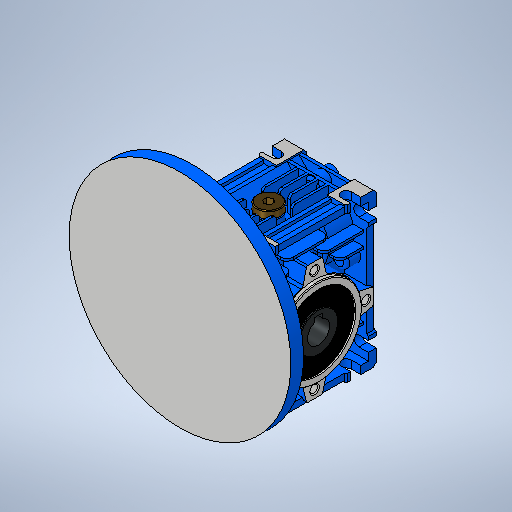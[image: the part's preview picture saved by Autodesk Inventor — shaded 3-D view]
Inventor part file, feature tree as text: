
AUTODESK INVENTOR PART (.ipt)
format: ipt  version: 2025.1 (Build 291241020, 241B)  size: 3,167,232 bytes
history: native  units: mm
features: extrude x72, sketch x64, projected_geometry x30, chamfer x22, fillet x17, mirror x13, other x8, hole x3, pattern_linear x1, revolve x1, sheet_metal_op x1
ambient origin geometry x8: Origin, YZ Plane, XZ Plane, XY Plane, X Axis, Y Axis, Z Axis, Center Point
bodies: Body1 (feature_tree), Body2 (feature_tree), Body3 (feature_tree)
feature tree (232):
  other  "Твердое тело1"
  extrude  "Выдавливание1"  Depth=63.0mm
  extrude  "Выдавливание2"  Depth=55.0mm
  extrude  "Выдавливание3"  Depth=15.0mm
  mirror  "Зеркальное отражение2"
  mirror  "Зеркальное отражение3"
  mirror  "Зеркальное отражение4"
  hole  "Отверстие1"  [1 undecoded]
  mirror  "Зеркальное отражение5"
  extrude  "Выдавливание4"  Depth=15.0mm
  extrude  "Выдавливание5"  Depth=15.0mm
  mirror  "Зеркальное отражение6"
  extrude  "Выдавливание6"  Depth=15.0mm
  mirror  "Зеркальное отражение7"
  chamfer  "Фаска1"  Distance=32.5mm
  extrude  "Выдавливание8"  Depth=10.0mm
  extrude  "Выдавливание9"  Depth=15.0mm
  fillet  "Сопряжение1"  Radius=1.0mm
  mirror  "Зеркальное отражение8"
  extrude  "Выдавливание10"  Depth=15.0mm
  extrude  "Выдавливание11"  Depth=15.0mm TaperAngle=360.0deg
  extrude  "Выдавливание12"  Depth=15.0mm TaperAngle=0.0deg
  chamfer  "Фаска2"  Distance=32.5mm
  chamfer  "Фаска3"  Distance=32.5mm
  extrude  "Выдавливание13"  Depth=15.0mm
  extrude  "Выдавливание14"  Depth=15.0mm
  chamfer  "Фаска4"  Distance=14.0mm
  extrude  "Выдавливание15"  Depth=5.0mm
  mirror  "Зеркальное отражение9"
  other  "РабПлоскость1"
  extrude  "Выдавливание16"  Depth=15.0mm
  extrude  "Выдавливание17"  Depth=15.0mm TaperAngle=0.0deg
  pattern_linear  "Прямоуг.массив1"  Spacing1=25.0mm  [1 undecoded]
  chamfer  "Фаска6"  Distance=47.0mm
  extrude  "Выдавливание18"  Depth=15.0mm TaperAngle=0.0deg
  chamfer  "Фаска7"  Distance=42.0mm
  fillet  "Сопряжение2"  Radius=42.0mm
  fillet  "Сопряжение3"  Radius=58.0mm
  fillet  "Сопряжение4"  Radius=1.0mm
  extrude  "Выдавливание19"  Depth=5.0mm
  chamfer  "Фаска8"  Distance=5.0mm
  chamfer  "Фаска9"  Distance=58.0mm
  chamfer  "Фаска10"  Distance=2.0mm Angle=45.0deg
  other  "РабОсь1"
  extrude  "Выдавливание20"  Depth=15.0mm TaperAngle=0.0deg
  extrude  "Выдавливание21"  Depth=15.0mm
  chamfer  "Фаска13"  Distance=1.5mm
  fillet  "Сопряжение7"  Radius=8.0mm
  extrude  "Выдавливание22"  Depth=15.0mm
  chamfer  "Фаска14"  Distance=4.0mm
  extrude  "Выдавливание23"  Depth=15.0mm TaperAngle=0.0deg
  extrude  "Выдавливание26"  Depth=15.0mm
  extrude  "Выдавливание27"  Depth=15.0mm TaperAngle=0.0deg
  chamfer  "Фаска15"  Distance=1.0mm
  extrude  "Выдавливание28"  Depth=15.0mm
  chamfer  "Фаска16"  Distance=1.0mm
  extrude  "Выдавливание29"  Depth=15.0mm TaperAngle=45.0deg
  chamfer  "Фаска17"  Distance=0.4mm Angle=45.0deg
  chamfer  "Фаска18"  Distance=20.0mm
  extrude  "Выдавливание30"  Depth=15.0mm TaperAngle=0.0deg
  mirror  "Зеркальное отражение10"
  extrude  "Выдавливание32"  Depth=15.0mm TaperAngle=0.0deg
  mirror  "Зеркальное отражение11"
  extrude  "Выдавливание33"  Depth=15.0mm TaperAngle=45.0deg
  extrude  "Выдавливание34"  Depth=15.0mm
  fillet  "Сопряжение8"  Radius=2.5mm
  extrude  "Выдавливание35"  Depth=15.0mm TaperAngle=0.0deg
  fillet  "Сопряжение10"  [1 undecoded]
  extrude  "Выдавливание36"  Depth=15.0mm
  fillet  "Сопряжение12"  Radius=1.5mm
  extrude  "Выдавливание37"  Depth=15.0mm TaperAngle=0.0deg
  extrude  "Выдавливание38"  Depth=15.0mm TaperAngle=0.0deg
  extrude  "Выдавливание39"  Depth=15.0mm
  chamfer  "Фаска19"  Distance=4.0mm Angle=45.0deg
  extrude  "Выдавливание40"  Depth=15.0mm TaperAngle=0.0deg
  sketch  "Эскиз45"
  extrude  "Выдавливание41"  Depth=15.0mm TaperAngle=45.0deg
  extrude  "Выдавливание42"  Depth=15.0mm
  extrude  "Выдавливание43"  Depth=15.0mm
  extrude  "Выдавливание44"  Depth=15.0mm
  extrude  "Выдавливание45"  Depth=15.0mm
  fillet  "Сопряжение13"  Radius=6.5mm
  other  "РабПлоскость2"
  extrude  "Выдавливание46"  Depth=15.0mm
  other  "РабПлоскость3"
  other  "РабПлоскость4"
  sketch  "Эскиз49"
  extrude  "Выдавливание47"  Depth=15.0mm
  extrude  "Выдавливание48"  Depth=15.0mm
  fillet  "Сопряжение14"  Radius=44.0mm
  extrude  "Выдавливание49"  Depth=15.0mm TaperAngle=0.0deg
  fillet  "Сопряжение15"  Radius=1.0mm
  extrude  "Выдавливание50"  Depth=15.0mm TaperAngle=45.0deg
  extrude  "Выдавливание51"  Depth=15.0mm TaperAngle=45.0deg
  extrude  "Выдавливание52"  Depth=15.0mm
  extrude  "Выдавливание53"  Depth=15.0mm
  extrude  "Выдавливание54"  Depth=4.0mm
  fillet  "Сопряжение16"  Radius=4.0mm
  extrude  "Выдавливание55"  Depth=4.0mm
  extrude  "Выдавливание56"  TaperAngle=120.0deg  [1 undecoded]
  chamfer  "Фаска20"  Angle=120.0deg  [1 undecoded]
  hole  "Отверстие2"  [1 undecoded]
  extrude  "Выдавливание57"  Depth=15.0mm
  chamfer  "Фаска21"  Distance=3.0mm
  extrude  "Выдавливание58"  Depth=15.0mm
  extrude  "Выдавливание59"  Depth=15.0mm
  extrude  "Выдавливание60"  Depth=15.0mm
  extrude  "Выдавливание61"  Depth=15.0mm
  extrude  "Выдавливание62"  Depth=15.0mm
  extrude  "Выдавливание63"  Depth=15.0mm TaperAngle=0.0deg
  extrude  "Выдавливание64"  Depth=15.0mm
  chamfer  "Фаска22"  Distance=1.0mm
  fillet  "Сопряжение17"  Radius=0.0001mm
  extrude  "Выдавливание65"  Depth=15.0mm TaperAngle=45.0deg
  mirror  "Зеркальное отражение13"
  extrude  "Выдавливание66"  Depth=15.0mm
  chamfer  "Фаска24"  Distance=17.75mm
  extrude  "Выдавливание67"  Depth=15.0mm TaperAngle=45.0deg
  chamfer  "Фаска25"  Distance=28.5mm
  extrude  "Выдавливание68"  Depth=15.0mm
  mirror  "Зеркальное отражение14"
  extrude  "Выдавливание69"  Depth=5.5mm
  chamfer  "Фаска26"  Distance=3.0mm
  extrude  "Выдавливание70"  Depth=15.0mm
  extrude  "Выдавливание72"  Depth=15.0mm TaperAngle=0.0deg
  fillet  "Сопряжение18"  Radius=2.0mm
  extrude  "Выдавливание73"  Depth=15.0mm TaperAngle=45.0deg
  fillet  "Сопряжение19"  Radius=32.0mm
  extrude  "Выдавливание74"  Depth=15.0mm TaperAngle=0.0deg
  fillet  "Сопряжение20"  Radius=0.5mm
  hole  "Отверстие4"  [1 undecoded]
  other  "РабПлоскость6"
  extrude  "Выдавливание76"  Depth=4.0mm
  mirror  "Зеркальное отражение15"
  fillet  "Сопряжение21"  Radius=4.0mm
  extrude  "Выдавливание77"  Depth=15.0mm TaperAngle=0.0deg
  extrude  "Выдавливание78"  Depth=15.0mm TaperAngle=45.0deg
  revolve  "Revolution1"  Angle=45.0deg
  sketch  "Эскиз1"
  sketch  "Sketch Circular Pattern1"  dims[d0=80.0mm d1=63.0mm]
  sketch  "Эскиз4"
  projected_geometry  "Спроецированная петля3"
  sketch  "Эскиз10"
  projected_geometry  "Спроецированная петля5"
  sketch  "Эскиз11"
  sketch  "Эскиз12"
  sketch  "Эскиз13"
  sketch  "Эскиз18"
  sketch  "Эскиз19"
  projected_geometry  "Спроецированная петля6"
  sketch  "Эскиз20"
  projected_geometry  "Спроецированная петля7"
  sketch  "Эскиз22"
  sketch  "Эскиз26"
  sketch  "Эскиз27"
  sketch  "Эскиз28"
  sketch  "Эскиз29"
  projected_geometry  "Спроецированная петля9"
  projected_geometry  "Спроецированная петля10"
  sketch  "Эскиз30"
  projected_geometry  "Спроецированная петля11"
  sketch  "Эскиз31"
  projected_geometry  "Спроецированная петля12"
  sketch  "Эскиз32"
  projected_geometry  "Спроецированная петля13"
  sketch  "Эскиз34"
  projected_geometry  "Спроецированная петля14"
  sketch  "Эскиз35"
  sketch  "Эскиз36"
  sketch  "Эскиз37"
  sketch  "Эскиз38"
  sketch  "Эскиз39"
  sketch  "Эскиз40"
  sketch  "Эскиз42"
  sketch  "Эскиз43"
  sketch  "Эскиз46"
  projected_geometry  "Спроецированная петля15"
  sketch  "Эскиз47"
  sketch  "Эскиз48"
  projected_geometry  "Спроецированная петля16"
  sketch  "Эскиз50"
  sketch  "Эскиз51"
  sketch  "Эскиз53"
  sketch  "Эскиз54"
  projected_geometry  "Спроецированная петля23"
  projected_geometry  "Спроецированная петля24"
  sketch  "Эскиз55"
  sketch  "Эскиз56"
  projected_geometry  "Спроецированная петля25"
  projected_geometry  "Спроецированная петля26"
  sketch  "Эскиз57"
  sketch  "Эскиз58"
  projected_geometry  "Спроецированная петля27"
  sketch  "Эскиз59"
  sketch  "Эскиз60"
  other  "Твердое тело4"
  sketch  "Эскиз61"
  sketch  "Эскиз62"
  projected_geometry  "Спроецированная петля28"
  projected_geometry  "Спроецированная петля29"
  sketch  "Эскиз63"
  sketch  "Эскиз64"
  sketch  "Sketch Circular Pattern2"  dims[d2=97.0mm d3=0.0mm d4=55.0mm]
  sketch  "Эскиз65"
  projected_geometry  "Спроецированная петля30"
  sketch  "Эскиз66"
  sketch  "Эскиз67"
  projected_geometry  "Спроецированная петля31"
  sketch  "Эскиз69"
  sketch  "Эскиз71"
  sketch  "Эскиз72"
  projected_geometry  "Спроецированная петля34"
  projected_geometry  "Спроецированная петля35"
  sketch  "Эскиз73"
  sketch  "Эскиз74"
  projected_geometry  "Спроецированная петля36"
  sketch  "Эскиз75"
  sketch  "Эскиз78"
  sketch  "Эскиз79"
  projected_geometry  "Спроецированная петля38"
  sketch  "Эскиз83"
  sketch  "Эскиз84"
  sketch  "Эскиз86"
  sketch  "Эскиз87"
  projected_geometry  "Спроецированная петля39"
  projected_geometry  "Спроецированная петля40"
  projected_geometry  "Спроецированная петля41"
  projected_geometry  "Спроецированная петля42"
  sketch  "Эскиз88"
  projected_geometry  "Спроецированная петля43"
  sketch  "Sketch90"  dims[d5=40.0mm d6=40.0mm d7=2.5mm d8=0.0mm d9=2.5mm d12=56.0mm d13=6.0mm d14=32.5mm d15=10.0mm d16=15.0mm d17=1.0mm d18=2.0mm d19=40.0mm d21=360.0deg d23=1.0mm d24=0.0mm d25=32.5mm d26=32.5mm d27=32.5mm d28=32.5mm d29=4.917mm d30=11.0mm d31=6.0mm d32=2.0mm d33=90.0deg d34=12.0mm d35=20.594885mm d36=14.0mm d37=5.0mm d38=16.3mm d39=1.0mm d40=0.0mm d41=25.0mm d42=47.0mm d43=1.0mm d44=0.0mm d45=42.0mm d46=42.0mm d47=58.0mm d49=1.0mm d50=0.0mm d51=5.0mm d52=5.0mm d53=58.0mm d54=2.0mm d55=2.0mm d56=45.0deg d59=14.0mm d60=0.0mm d61=8.0mm d62=1.5mm d63=8.0mm d64=1.5mm d65=4.0mm d66=12.0mm d67=0.0mm d68=2.0mm d69=1.0mm d70=0.0mm d71=1.0mm d72=0.0mm d73=32.0mm d74=1.0mm d75=0.0mm d76=0.4mm d77=2.0mm d78=45.0deg d79=0.4mm d80=2.0mm d81=45.0deg d82=20.0mm d83=32.25mm d84=0.0mm d85=22.0mm d86=0.0mm d87=6.0mm d88=2.0mm d89=45.0deg d95=3.0mm d96=2.5mm d97=2.0mm d98=0.0mm d99=-7.0mm d102=72.0mm d103=1.5mm d104=35.0mm d105=0.0mm d106=2.5mm d107=0.0mm d108=40.0mm d110=6.1666mm d111=4.0mm d112=2.0mm d113=45.0deg d114=2.5mm d115=0.0mm d116=8.0mm d117=2.0mm d118=45.0deg d119=2.0mm d120=2.0mm d121=2.0mm d123=6.5mm d124=6.5mm d125=6.5mm d126=6.5mm d127=54.0mm d128=44.0mm d129=6.0mm d130=0.0mm d131=1.0mm d132=2.0mm d133=45.0deg d134=2.0mm d135=2.0mm d136=45.0deg d137=0.5mm d138=2.0mm d139=45.0deg d140=30.0mm d141=38.0mm d142=4.0mm d143=4.0mm d144=4.0mm d145=120.0deg d146=120.0deg d147=120.0deg d149=3.0mm d150=3.0mm d151=3.0mm d152=19.0mm d153=19.0mm d154=19.0mm d155=2.0mm d156=2.0mm d158=32.0mm d159=1.0mm d160=0.0mm d161=1.0mm d162=1.0mm d163=0.0mm d170=0.0001mm d171=6.0mm d172=2.0mm d173=45.0deg d175=2.0mm d176=17.75mm d177=0.0mm d178=6.0mm d179=2.0mm d180=45.0deg d181=28.5mm d182=0.0mm d183=3.0mm d184=5.5mm d189=3.0mm d190=0.5mm d191=2.0mm d192=0.0mm d193=2.0mm d194=0.0mm d195=1.0mm d196=2.0mm d197=45.0deg d198=32.0mm d199=1.0mm d200=0.0mm d201=0.5mm d202=2.0mm d203=45.0deg d204=4.0mm d205=4.0mm d206=4.0mm d207=12.0mm d208=0.0mm d209=0.5mm d210=2.0mm d211=45.0deg d212=2.0mm d213=2.0mm d214=45.0deg d215=14.0mm d216=0.0mm d219=15.0mm d220=10.0mm d221=0.0mm d222=10.0mm d223=0.0mm d224=43.0mm d225=18.0mm d226=0.0mm d227=2.0mm d228=18.0mm d229=0.0mm d231=2.0mm d233=9.0mm d234=0.0mm d235=2.0mm d236=6.5mm d237=6.5mm d238=6.5mm d239=6.5mm d240=44.0mm d241=71.0mm d243=44.0mm d244=27.0mm d245=22.0mm d246=9.0mm d247=0.0mm d248=9.0mm d249=0.0mm d250=9.0mm d251=0.0mm d252=1.0mm d253=2.0mm d254=45.0deg d255=2.0mm d256=10.0mm d257=32.0mm d258=4.0mm d259=0.0mm d260=6.0mm d261=6.0mm d262=90.0deg d263=3.5mm d264=0.0mm d265=1.0mm d266=90.0deg d267=3.5mm d268=0.0mm d269=3.5mm d270=0.0mm d271=5.0mm d272=0.0mm d273=5.0mm d274=0.0mm d275=2.0mm d276=5.5mm d277=2.0mm d278=0.0mm d279=10.5mm d280=8.0mm d281=6.75mm d282=0.0mm d283=2.0mm d284=0.0mm d285=2.0mm d286=6.25mm d287=0.0mm d288=2.0mm d289=20.0mm d290=1.5mm d291=1.5mm d292=1.5mm d293=1.5mm d294=7.1mm d295=0.0mm d296=14.6mm d297=0.0mm d298=7.1mm d299=0.0mm d300=7.1mm d301=0.0mm d302=7.1mm d303=0.0mm d304=2.0mm d305=15.0mm d306=16.35mm d307=0.0mm d308=5.0mm d309=0.0mm d310=0.5mm d311=2.0mm d312=45.0deg d313=8.376mm d314=10.0mm d315=10.0mm d316=2.0mm d317=90.0deg d318=15.0mm d319=20.594885mm d320=5.0mm d321=0.0mm d322=0.5mm d323=2.0mm d324=45.0deg d325=5.0mm d326=4.0mm d327=0.0mm d328=2.0mm d329=0.0mm d330=2.0mm d331=0.0mm d332=43.0mm d333=6.0mm d334=22.5mm d335=37.0mm d336=2.0mm d337=40.0mm d339=360.0deg d341=1.0mm d342=0.0mm d343=1.0mm d344=0.0mm d345=1.0mm d346=0.0mm d347=1.0mm d348=0.0mm d349=6.0mm d350=2.0mm d351=45.0deg d352=2.0mm d355=2.0mm d356=0.0mm d360=1.0mm d361=0.0mm d362=1.0mm d363=2.0mm d364=45.0deg d365=2.0mm d366=2.0mm d367=45.0deg d368=1.0mm d369=0.0mm d370=9.0mm d371=15.0mm d372=3.0mm d373=0.0mm d374=7.0mm d375=0.0mm d376=0.5mm d377=2.0mm d378=45.0deg d379=20.0mm d380=16.0mm d381=0.0mm d388=11.0mm d390=13.0mm d391=4.0mm d392=30.0mm d393=0.0mm d394=1.0mm d395=1.5mm d396=1.5mm d397=0.5mm d398=0.0mm d399=3.0mm d409=2.0mm d410=3.0mm d411=3.0mm d412=3.0mm d413=3.0mm d414=8.0mm d415=0.0mm d416=2.0mm d417=4.917mm d418=11.0mm d419=6.0mm d420=2.0mm d421=90.0deg d422=12.0mm d423=20.594885mm d435=-2.0mm d436=25.0mm d437=1.5mm d438=16.8mm d439=15.0mm d440=1.5mm d441=7.4mm d442=27.0mm d443=1.5mm d444=6.0mm d445=8.0mm d446=0.0mm d447=4.0mm d448=8.0mm d449=0.0mm d450=8.0mm d451=0.0mm d455=15.0mm d456=8.0mm d457=140.0mm d458=90.0deg]
  sheet_metal_op  "Flange"
note: 7 required parameter values undecoded (feature->parameter linkage not recoverable at this tier; creation-order binding heuristic only, values carry confidence <= 0.55)
